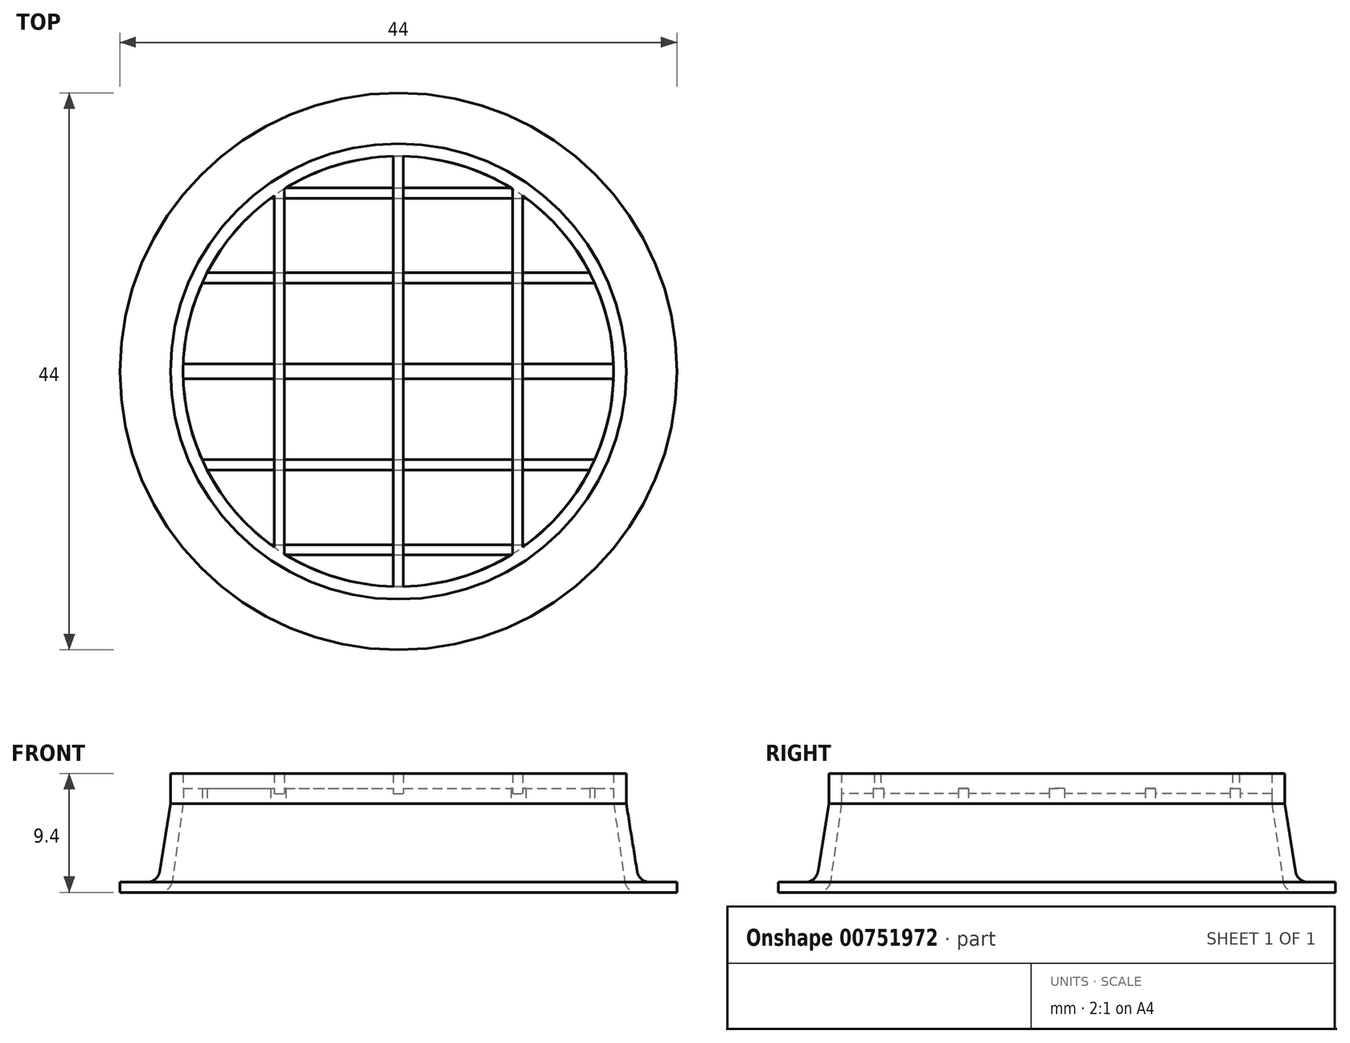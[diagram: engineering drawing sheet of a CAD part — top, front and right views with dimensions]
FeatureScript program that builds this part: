
annotation { "Feature Type Name" : "Feature", "Feature Type Description" : "" }
export const myFeature = defineFeature(function(context is Context, id is Id, definition is map)
    precondition{}
    {
        {
            var Q0;
            Q0=qCreatedBy(makeId("Front.planeOp"),FACE);
            var sketch = newSketch(context, id + "F0", { "sketchPlane" : qUnion([Q0])});
            skLineSegment(sketch, "E0", {"start": v(0, 16.66) * mm, "end": v(0, -15.75) * mm, "construction": true});
            skLineSegment(sketch, "E1", {"start": v(8.08, 0) * mm, "end": v(-29.3, 0) * mm, "construction": true});
            skLineSegment(sketch, "E2", {"start": v(1.58, 0) * mm, "end": v(-1.66, 0) * mm, "construction": true});
            skLineSegment(sketch, "E3", {"start": v(-1, 1.45) * mm, "end": v(-1, -7.95) * mm, "construction": true});
            skLineSegment(sketch, "E4", {"start": v(-5, -6.2) * mm, "end": v(-5, -8.06) * mm, "construction": true});
            skLineSegment(sketch, "E5", {"start": v(-5, -7) * mm, "end": v(-1.87, -7) * mm});
            skLineSegment(sketch, "E6", {"start": v(-0.88, -6.14) * mm, "end": v(0, 0) * mm});
            skLineSegment(sketch, "E7", {"start": v(0, 0) * mm, "end": v(-1, 0) * mm});
            skLineSegment(sketch, "E8", {"start": v(-1, 0) * mm, "end": v(-1.86, -5.36) * mm});
            skLineSegment(sketch, "E9", {"start": v(-2.85, -6.2) * mm, "end": v(-5, -6.2) * mm});
            skLineSegment(sketch, "E10", {"start": v(-5, -6.2) * mm, "end": v(-5, -7) * mm});
            skPoint(sketch, "E11.visualSharp", {"position": v(-2, -6.2) * mm});
            skArc(sketch, "E11.filletArc", {"start": v(-2.85, -6.2) * mm, "mid": v(-2.2, -5.96) * mm, "end": v(-1.86, -5.36) * mm});
            skPoint(sketch, "E12.visualSharp", {"position": v(-1, -7) * mm});
            skArc(sketch, "E12.filletArc", {"start": v(-1.87, -7) * mm, "mid": v(-1.21, -6.76) * mm, "end": v(-0.88, -6.14) * mm});
            skLineSegment(sketch, "E13", {"start": v(17, 0.36) * mm, "end": v(17, -7.36) * mm, "construction": true});
            skSolve(sketch);
        }
        {
            var Q0;
            Q0=qSketchRegion(id+"F0",true);
            var Q1;
            Q1=sQuery(id+"F0.wireOp",EDGE,"E13");
            revolve(context, id + "F1", {"surfaceOperationType" : NewSurfaceOperationType.NEW, "entities" : qUnion([Q0]), "axis" : qUnion([Q1]), "revolveType" : RevolveType.FULL});
        }
        {
            var Q0;
            Q0=makeQuery(id+"F1.opRevolve","SWEPT_FACE",FACE,{"disambiguationData":[OSD([sQuery(id+"F0.wireOp",EDGE,"E7")])]});
            var sketch = newSketch(context, id + "F2", { "sketchPlane" : qUnion([Q0])});
            skLineSegment(sketch, "E14", {"start": v(0, 0) * mm, "end": v(34, 0) * mm, "construction": true});
            skCircle(sketch, "E15.0", {"center": v(17, 0) * mm, "radius": 18 * mm});
            skLineSegment(sketch, "E16", {"start": v(-0.99, 0.6) * mm, "end": v(34.99, 0.6) * mm});
            skLineSegment(sketch, "E17", {"start": v(0.77, 7.78) * mm, "end": v(33.23, 7.78) * mm});
            skLineSegment(sketch, "E18", {"start": v(6.31, 14.49) * mm, "end": v(27.69, 14.49) * mm});
            skLineSegment(sketch, "E19", {"start": v(5.3, 13.69) * mm, "end": v(28.7, 13.69) * mm});
            skLineSegment(sketch, "E20.MirrorCS", {"start": v(-0.99, -0.6) * mm, "end": v(34.99, -0.6) * mm});
            skLineSegment(sketch, "E21.MirrorCS", {"start": v(0.77, -7.78) * mm, "end": v(33.23, -7.78) * mm});
            skLineSegment(sketch, "E22.MirrorCS", {"start": v(5.3, -13.69) * mm, "end": v(28.7, -13.69) * mm});
            skLineSegment(sketch, "E23.MirrorCS", {"start": v(6.31, -14.49) * mm, "end": v(27.69, -14.49) * mm});
            skLineSegment(sketch, "E24", {"start": v(0.4, 6.98) * mm, "end": v(33.6, 6.98) * mm});
            skLineSegment(sketch, "E25.MirrorCS", {"start": v(0.4, -6.98) * mm, "end": v(33.6, -6.98) * mm});
            skSolve(sketch);
        }
        {
            var Q0;
            {var subQ0=sQuery(id+"F2.wireOp",EDGE,"E18");var subQ1=makeQuery(id+"F1.opRevolve","SWEPT_EDGE",EDGE,{"disambiguationData":[OSD([sQuery(id+"F0.wireOp",EDGE,"E6"),sQuery(id+"F0.wireOp",EDGE,"E7")])]});var subQ2=makeQuery(id+"F2.imprint","INTERSECT",VERTEX,{"disambiguationData":[OD(0.0)],"derivedFrom":[subQ1,subQ0]});Q0=makeQuery(id+"F2.imprint","IMPRINT",FACE,{"disambiguationData":[TD([[makeQuery(id+"F2.imprint","IMPRINT",EDGE,{"disambiguationData":[TD([[subQ2,-1.0]])],"derivedFrom":subQ0}),-1.0]])]});}
            var Q1;
            {var subQ0=sQuery(id+"F2.wireOp",EDGE,"E17");var subQ1=makeQuery(id+"F1.opRevolve","SWEPT_EDGE",EDGE,{"disambiguationData":[OSD([sQuery(id+"F0.wireOp",EDGE,"E6"),sQuery(id+"F0.wireOp",EDGE,"E7")])]});var subQ2=makeQuery(id+"F2.imprint","INTERSECT",VERTEX,{"disambiguationData":[OD(0.0)],"derivedFrom":[subQ1,subQ0]});Q1=makeQuery(id+"F2.imprint","IMPRINT",FACE,{"disambiguationData":[TD([[makeQuery(id+"F2.imprint","IMPRINT",EDGE,{"disambiguationData":[TD([[subQ2,-1.0]])],"derivedFrom":subQ0}),-1.0]])]});}
            var Q2;
            {var subQ0=sQuery(id+"F2.wireOp",EDGE,"E16");var subQ1=makeQuery(id+"F1.opRevolve","SWEPT_EDGE",EDGE,{"disambiguationData":[OSD([sQuery(id+"F0.wireOp",EDGE,"E6"),sQuery(id+"F0.wireOp",EDGE,"E7")])]});var subQ2=makeQuery(id+"F2.imprint","INTERSECT",VERTEX,{"disambiguationData":[OD(0.0)],"derivedFrom":[subQ1,subQ0]});Q2=makeQuery(id+"F2.imprint","IMPRINT",FACE,{"disambiguationData":[TD([[makeQuery(id+"F2.imprint","IMPRINT",EDGE,{"disambiguationData":[TD([[subQ2,-1.0]])],"derivedFrom":subQ0}),-1.0]])]});}
            var Q3;
            {var subQ0=sQuery(id+"F2.wireOp",EDGE,"E21.MirrorCS");var subQ1=makeQuery(id+"F1.opRevolve","SWEPT_EDGE",EDGE,{"disambiguationData":[OSD([sQuery(id+"F0.wireOp",EDGE,"E6"),sQuery(id+"F0.wireOp",EDGE,"E7")])]});var subQ2=makeQuery(id+"F2.imprint","INTERSECT",VERTEX,{"disambiguationData":[OD(0.0)],"derivedFrom":[subQ1,subQ0]});Q3=makeQuery(id+"F2.imprint","IMPRINT",FACE,{"disambiguationData":[TD([[makeQuery(id+"F2.imprint","IMPRINT",EDGE,{"disambiguationData":[TD([[subQ2,-1.0]])],"derivedFrom":subQ0}),1.0]])]});}
            var Q4;
            {var subQ0=sQuery(id+"F2.wireOp",EDGE,"E22.MirrorCS");var subQ1=makeQuery(id+"F1.opRevolve","SWEPT_EDGE",EDGE,{"disambiguationData":[OSD([sQuery(id+"F0.wireOp",EDGE,"E6"),sQuery(id+"F0.wireOp",EDGE,"E7")])]});var subQ2=makeQuery(id+"F2.imprint","INTERSECT",VERTEX,{"disambiguationData":[OD(0.0)],"derivedFrom":[subQ1,subQ0]});Q4=makeQuery(id+"F2.imprint","IMPRINT",FACE,{"disambiguationData":[TD([[makeQuery(id+"F2.imprint","IMPRINT",EDGE,{"disambiguationData":[TD([[subQ2,-1.0]])],"derivedFrom":subQ0}),-1.0]])]});}
            extrude(context, id + "F3", {"entities" : qUnion([Q0, Q1, Q2, Q3, Q4]), "depth" : 1.2 * mm, "offsetDistance" : 25 * mm});
        }
        {
            var Q0;
            Q0=makeQuery(id+"F1.opRevolve","SWEPT_FACE",FACE,{"disambiguationData":[OSD([sQuery(id+"F0.wireOp",EDGE,"E7")])]});
            var sketch = newSketch(context, id + "F4", { "sketchPlane" : qUnion([Q0])});
            skCircle(sketch, "E26.0", {"center": v(17, 0) * mm, "radius": 17 * mm});
            skCircle(sketch, "E27.0", {"center": v(17, 0) * mm, "radius": 18 * mm});
            skSolve(sketch);
        }
        {
            var Q0;
            Q0 = qSketchRegion(id + "F4", true);
            extrude(context, id + "F5", {"entities" : qUnion([Q0]), "depth" : 1.2 * mm, "offsetDistance" : 25 * mm});
        }
        {
            var Q0;
            Q0=makeQuery(id+"F5.opExtrude","CAP_FACE",FACE,{"disambiguationData":[OSD([sQuery(id+"F4.wireOp",EDGE,"E26.0"),sQuery(id+"F4.wireOp",EDGE,"E27.0")])],"isStart":false});
            var sketch = newSketch(context, id + "F6", { "sketchPlane" : qUnion([Q0])});
            skLineSegment(sketch, "E28", {"start": v(17, 17) * mm, "end": v(17, -17) * mm, "construction": true});
            skLineSegment(sketch, "E29", {"start": v(17.4, 17) * mm, "end": v(17.4, -17) * mm});
            skLineSegment(sketch, "E30", {"start": v(26.01, 14.41) * mm, "end": v(26.01, -14.41) * mm});
            skLineSegment(sketch, "E31", {"start": v(26.81, 13.88) * mm, "end": v(26.81, -13.88) * mm});
            skLineSegment(sketch, "E32.MirrorCS", {"start": v(16.6, 17) * mm, "end": v(16.6, -17) * mm});
            skLineSegment(sketch, "E33.MirrorCS", {"start": v(7.99, 14.41) * mm, "end": v(7.99, -14.41) * mm});
            skLineSegment(sketch, "E34.MirrorCS", {"start": v(7.19, 13.88) * mm, "end": v(7.19, -13.88) * mm});
            skCircle(sketch, "E35.0", {"center": v(17, 0) * mm, "radius": 18 * mm});
            skCircle(sketch, "E36.0", {"center": v(17, 0) * mm, "radius": 17 * mm});
            skLineSegment(sketch, "E37", {"start": v(7.19, 13.88) * mm, "end": v(7.99, 14.41) * mm});
            skLineSegment(sketch, "E38", {"start": v(16.6, 17) * mm, "end": v(17.4, 17) * mm});
            skLineSegment(sketch, "E39", {"start": v(26.01, 14.41) * mm, "end": v(26.81, 13.88) * mm});
            skLineSegment(sketch, "E40", {"start": v(26.81, -13.88) * mm, "end": v(26.01, -14.41) * mm});
            skLineSegment(sketch, "E41", {"start": v(17.4, -17) * mm, "end": v(16.6, -17) * mm});
            skLineSegment(sketch, "E42", {"start": v(7.99, -14.41) * mm, "end": v(7.19, -13.88) * mm});
            skSolve(sketch);
        }
        {
            var Q0;
            Q0 = qSketchRegion(id + "F6", true);
            var Q1;
            Q1=makeQuery(id+"F6.imprint","IMPRINT",FACE,{"disambiguationData":[TD([[makeQuery(id+"F6.imprint","IMPRINT",EDGE,{"derivedFrom":sQuery(id+"F6.wireOp",EDGE,"E33.MirrorCS")}),-1.0]])]});
            var Q2;
            Q2=makeQuery(id+"F6.imprint","IMPRINT",FACE,{"disambiguationData":[TD([[makeQuery(id+"F6.imprint","IMPRINT",EDGE,{"derivedFrom":sQuery(id+"F6.wireOp",EDGE,"E29")}),-1.0]])]});
            var Q3;
            Q3=makeQuery(id+"F6.imprint","IMPRINT",FACE,{"disambiguationData":[TD([[makeQuery(id+"F6.imprint","IMPRINT",EDGE,{"derivedFrom":sQuery(id+"F6.wireOp",EDGE,"E30")}),1.0]])]});
            extrude(context, id + "F7", {"entities" : qUnion([Q0, Q1, Q2, Q3]), "operationType" : NewBodyOperationType.ADD, "depth" : 1.2 * mm, "offsetDistance" : 25 * mm, "hasSecondDirection" : true, "secondDirectionOppositeDirection" : true, "secondDirectionDepth" : .4 * mm});
        }
    });
